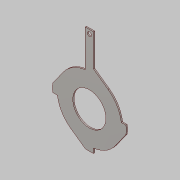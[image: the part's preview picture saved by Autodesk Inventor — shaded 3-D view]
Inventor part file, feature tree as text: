
AUTODESK INVENTOR PART (.ipt)
format: ipt  version: 2017 (Build 210142000, 142)  size: 143,360 bytes
history: native  units: mm
features: other x18, extrude x1, sketch x1
ambient origin geometry x8: Origin, YZ Plane, XZ Plane, XY Plane, X Axis, Y Axis, Z Axis, Center Point
bodies: Solid1 (feature_tree)
feature tree (20):
  other  "Table"
  other  "Part Number = Ground Plate Promag DN25"
  other  "Part Number = Ground Plate Promag DN32"
  other  "Part Number = Ground Plate Promag DN40"
  other  "Part Number = Ground Plate Promag DN50"
  other  "Part Number = Ground Plate Promag DN65"
  other  "Part Number = Ground Plate Promag DN80"
  other  "Part Number = Ground Plate Promag DN100"
  other  "Part Number = Ground Plate Promag DN125"
  other  "Part Number = Ground Plate Promag DN150"
  other  "Part Number = Ground Plate Promag DN200"
  other  "Part Number = Ground Plate Promag DN250"
  other  "Part Number = Ground Plate Promag DN300"
  other  "Part Number = Ground Plate Promag DN350"
  other  "Part Number = Ground Plate Promag DN400"
  other  "Part Number = Ground Plate Promag DN450"
  other  "Part Number = Ground Plate Promag DN500"
  other  "Part Number = Ground Plate Promag DN600"
  extrude  "Extrusion1"  Depth=13.0mm
  sketch  "Sketch1"  dims[d2=13.0mm d5=13.0mm d6=6.5mm d7=6.5mm d8=13.0mm d9=6.5mm d10=13.0mm d11=6.5mm d12=6.5mm d13=6.5mm d14=2.0mm d15=0.0mm d16=0.0mm]
